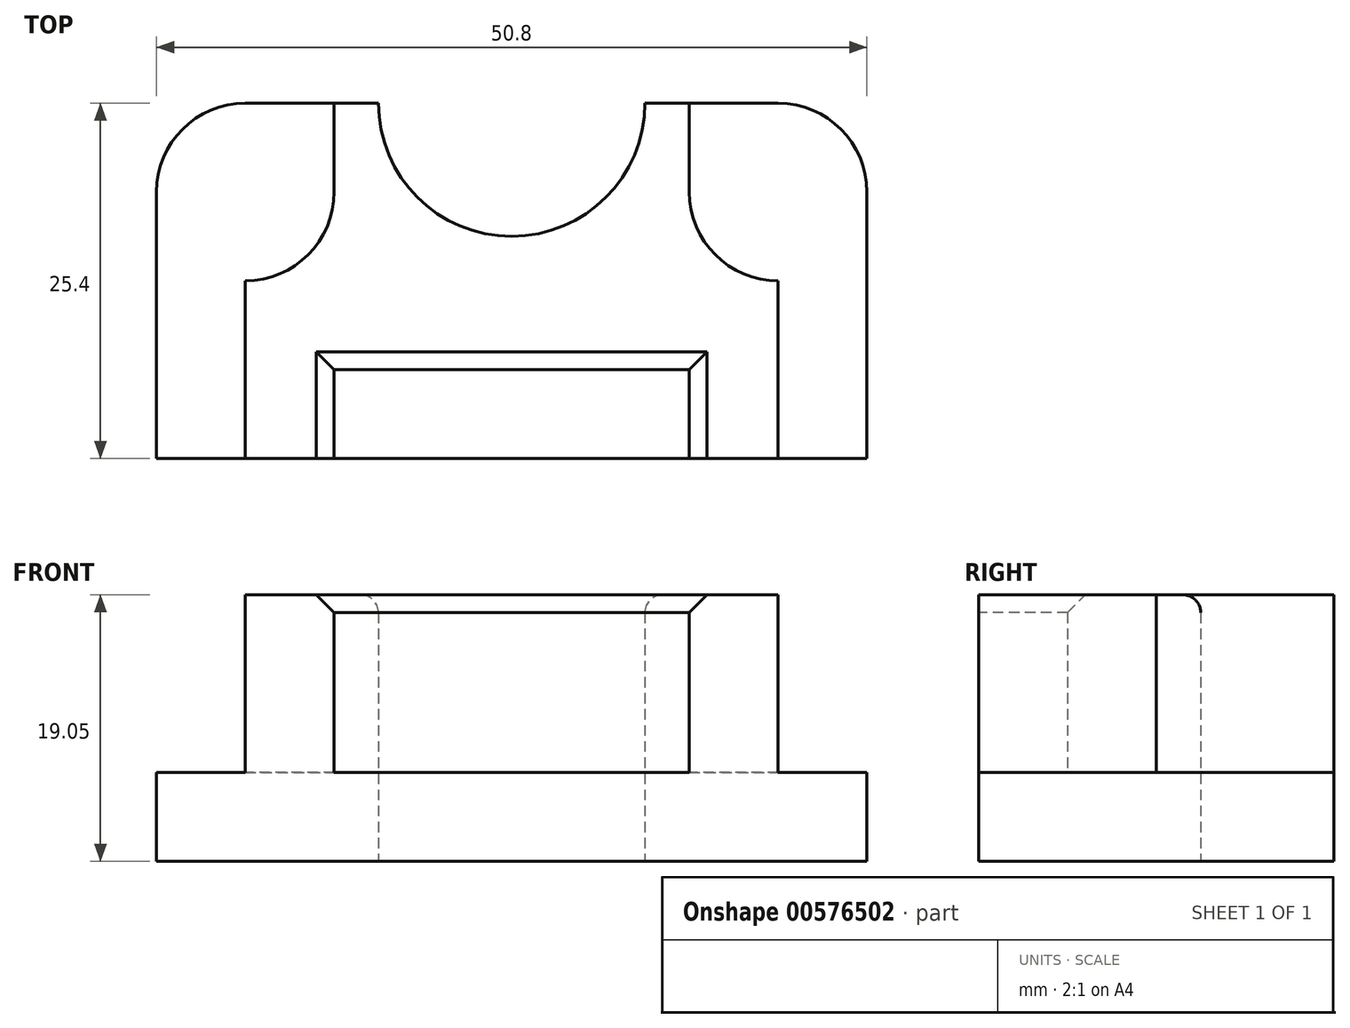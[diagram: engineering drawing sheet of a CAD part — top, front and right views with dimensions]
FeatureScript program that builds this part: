
annotation { "Feature Type Name" : "Feature", "Feature Type Description" : "" }
export const myFeature = defineFeature(function(context is Context, id is Id, definition is map)
    precondition{}
    {
        {
            var Q0;
            Q0=qCreatedBy(makeId("Top.planeOp"),FACE);
            var sketch = newSketch(context, id + "F0", { "sketchPlane" : qUnion([Q0])});
            skLineSegment(sketch, "E0.bottom", {"start": v(19.05, 12.7) * mm, "end": v(-19.05, 12.7) * mm});
            skLineSegment(sketch, "E0.top", {"start": v(25.4, -12.7) * mm, "end": v(-25.4, -12.7) * mm});
            skLineSegment(sketch, "E0.left", {"start": v(25.4, 6.35) * mm, "end": v(25.4, -12.7) * mm});
            skLineSegment(sketch, "E0.right", {"start": v(-25.4, 6.35) * mm, "end": v(-25.4, -12.7) * mm});
            skPoint(sketch, "E0.middle", {"position": v(0, 0) * mm});
            skPoint(sketch, "E1.visualSharp", {"position": v(-25.4, 12.7) * mm});
            skArc(sketch, "E1.filletArc", {"start": v(-19.05, 12.7) * mm, "mid": v(-23.54, 10.84) * mm, "end": v(-25.4, 6.35) * mm});
            skPoint(sketch, "E2.visualSharp", {"position": v(25.4, 12.7) * mm});
            skArc(sketch, "E2.filletArc", {"start": v(25.4, 6.35) * mm, "mid": v(23.54, 10.84) * mm, "end": v(19.05, 12.7) * mm});
            skSolve(sketch);
        }
        {
            var Q0;
            Q0=makeQuery(id+"F0.imprint","IMPRINT",FACE,{"disambiguationData":[TD([[makeQuery(id+"F0.imprint","IMPRINT",EDGE,{"derivedFrom":sQuery(id+"F0.wireOp",EDGE,"E0.bottom")}),1.0]])]});
            extrude(context, id + "F1", {"entities" : qUnion([Q0]), "depth" : 6.35 * mm, "offsetDistance" : 25.4 * mm});
        }
        {
            var Q0;
            Q0=makeQuery(id+"F1.opExtrude","CAP_FACE",FACE,{"disambiguationData":[OSD([sQuery(id+"F0.wireOp",EDGE,"E0.bottom"),sQuery(id+"F0.wireOp",EDGE,"E0.top"),sQuery(id+"F0.wireOp",EDGE,"E0.left"),sQuery(id+"F0.wireOp",EDGE,"E0.right")])],"isStart":false});
            var sketch = newSketch(context, id + "F2", { "sketchPlane" : qUnion([Q0])});
            skLineSegment(sketch, "E3.top", {"start": v(-25.4, 12.7) * mm, "end": v(19.05, 12.7) * mm});
            skLineSegment(sketch, "E3.left", {"start": v(-25.4, -12.7) * mm, "end": v(-25.4, 12.7) * mm});
            skLineSegment(sketch, "E3.right", {"start": v(19.05, -12.7) * mm, "end": v(19.05, 12.7) * mm});
            skLineSegment(sketch, "E4.bottom", {"start": v(-19.05, -12.7) * mm, "end": v(19.05, -12.7) * mm});
            skLineSegment(sketch, "E4.top", {"start": v(-19.05, 12.7) * mm, "end": v(19.05, 12.7) * mm});
            skLineSegment(sketch, "E5", {"start": v(-19.05, -12.7) * mm, "end": v(-12.7, -12.7) * mm});
            skLineSegment(sketch, "E6", {"start": v(19.05, -12.7) * mm, "end": v(12.7, -12.7) * mm});
            skLineSegment(sketch, "E7", {"start": v(-12.7, 6.35) * mm, "end": v(-12.7, 12.7) * mm});
            skLineSegment(sketch, "E8", {"start": v(12.7, 6.35) * mm, "end": v(12.7, 12.7) * mm});
            skCircle(sketch, "E9", {"center": v(0, 12.7) * mm, "radius": 9.53 * mm});
            skLineSegment(sketch, "E10", {"start": v(-19.05, 0) * mm, "end": v(-19.05, 0) * mm});
            skLineSegment(sketch, "E11", {"start": v(19.05, 0) * mm, "end": v(19.05, 0) * mm});
            skLineSegment(sketch, "E12", {"start": v(-9.53, 12.7) * mm, "end": v(9.52, 12.7) * mm});
            skLineSegment(sketch, "E13", {"start": v(-12.7, -12.7) * mm, "end": v(-12.7, -6.35) * mm});
            skLineSegment(sketch, "E14", {"start": v(-12.7, -6.35) * mm, "end": v(12.7, -6.35) * mm});
            skLineSegment(sketch, "E15", {"start": v(-19.05, -12.7) * mm, "end": v(-19.05, 0) * mm});
            skLineSegment(sketch, "E16", {"start": v(19.05, 0) * mm, "end": v(19.05, -12.7) * mm});
            skPoint(sketch, "E17.newPointA", {"position": v(-12.7, -12.7) * mm});
            skPoint(sketch, "E17.newPointB", {"position": v(-12.7, 0) * mm});
            skArc(sketch, "E17.filletArc", {"start": v(-19.05, 0) * mm, "mid": v(-14.56, 1.86) * mm, "end": v(-12.7, 6.35) * mm});
            skPoint(sketch, "E18.newPointA", {"position": v(12.7, -12.7) * mm});
            skPoint(sketch, "E18.newPointB", {"position": v(12.7, 0) * mm});
            skArc(sketch, "E18.filletArc", {"start": v(12.7, 6.35) * mm, "mid": v(14.56, 1.86) * mm, "end": v(19.05, 0) * mm});
            skLineSegment(sketch, "E19", {"start": v(12.7, -12.7) * mm, "end": v(12.7, -6.35) * mm});
            skLineSegment(sketch, "E20", {"start": v(12.7, -12.7) * mm, "end": v(19.05, -12.7) * mm});
            skLineSegment(sketch, "E21", {"start": v(9.52, 12.7) * mm, "end": v(12.7, 12.7) * mm});
            skLineSegment(sketch, "E22", {"start": v(-12.7, 12.7) * mm, "end": v(-9.53, 12.7) * mm});
            skSolve(sketch);
        }
        {
            var Q0;
            Q0=makeQuery(id+"F2.imprint","IMPRINT",FACE,{"disambiguationData":[TD([[makeQuery(id+"F2.imprint","IMPRINT",EDGE,{"derivedFrom":sQuery(id+"F2.wireOp",EDGE,"E7")}),-1.0]])]});
            extrude(context, id + "F3", {"entities" : qUnion([Q0]), "operationType" : NewBodyOperationType.ADD, "depth" : 12.7 * mm, "offsetDistance" : 25.4 * mm});
        }
        {
            var Q0;
            {var subQ0=sQuery(id+"F0.wireOp",EDGE,"E0.bottom");Q0=makeQuery(id+"F3.boolean.opBoolean","SPLIT",FACE,{"disambiguationData":[TD([makeQuery(id+"F3.opExtrude","SWEPT_FACE",FACE,{"disambiguationData":[OSD([sQuery(id+"F2.wireOp",EDGE,"E9")])]})])],"derivedFrom":makeQuery(id+"F1.opExtrude","CAP_FACE",FACE,{"disambiguationData":[OSD([subQ0,sQuery(id+"F0.wireOp",EDGE,"E0.top"),sQuery(id+"F0.wireOp",EDGE,"E0.left"),sQuery(id+"F0.wireOp",EDGE,"E0.right")])],"isStart":false})});}
            var sketch = newSketch(context, id + "F4", { "sketchPlane" : qUnion([Q0])});
            skCircle(sketch, "E23", {"center": v(0, 12.7) * mm, "radius": 9.53 * mm});
            skSolve(sketch);
        }
        {
            var Q0;
            Q0 = qSketchRegion(id + "F4", true);
            extrude(context, id + "F5", {"entities" : qUnion([Q0]), "operationType" : NewBodyOperationType.REMOVE, "oppositeDirection" : true, "depth" : 25.4 * mm, "offsetDistance" : 25.4 * mm});
        }
        {
            var Q0;
            Q0=makeQuery(id+"F3.opExtrude","CAP_EDGE",EDGE,{"disambiguationData":[OSD([sQuery(id+"F2.wireOp",EDGE,"E9")])],"isStart":false});
            fillet(context, id + "F6", {"entities" : qUnion([Q0]), "radius" : 1.27 * mm, "tangentPropagation" : true, "allowEdgeOverflow" : false});
        }
        {
            var Q0;
            Q0=makeQuery(id+"F3.opExtrude","CAP_EDGE",EDGE,{"disambiguationData":[OSD([sQuery(id+"F2.wireOp",EDGE,"E14")])],"isStart":false});
            var Q1;
            Q1=makeQuery(id+"F3.opExtrude","CAP_EDGE",EDGE,{"disambiguationData":[OSD([sQuery(id+"F2.wireOp",EDGE,"E19")])],"isStart":false});
            var Q2;
            Q2=makeQuery(id+"F3.opExtrude","CAP_EDGE",EDGE,{"disambiguationData":[OSD([sQuery(id+"F2.wireOp",EDGE,"E13")])],"isStart":false});
            chamfer(context, id + "F7", {"entities" : qUnion([Q0, Q1, Q2]), "width" : 1.27 * mm, "tangentPropagation" : true});
        }
    });
